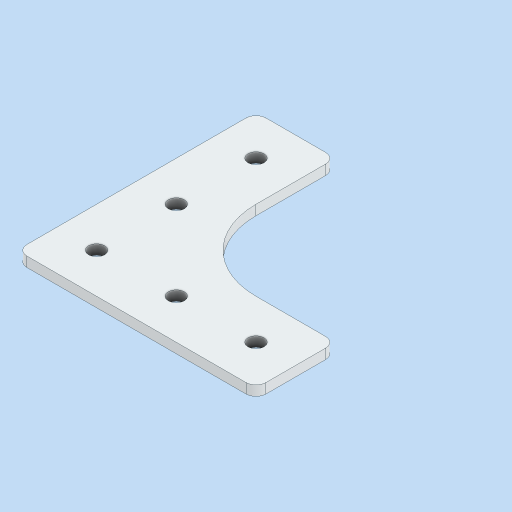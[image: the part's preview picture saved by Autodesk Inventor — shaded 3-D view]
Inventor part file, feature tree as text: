
AUTODESK INVENTOR PART (.ipt)
format: ipt  version: 2024 (Build 280153000, 153)  size: 113,152 bytes
history: native  units: in
note: dims shown in document units (in); Inventor stores cm internally (conversion verified against a paired STEP export)
features: fillet x1
ambient origin geometry x8: Origin, YZ Plane, XZ Plane, XY Plane, X Axis, Y Axis, Z Axis, Center Point
bodies: Solid1 (feature_tree)
feature tree (1):
  fillet  "Fillet1"  [1 undecoded]
note: 1 required parameter value undecoded (feature->parameter linkage not recoverable at this tier; creation-order binding heuristic only, values carry confidence <= 0.55)
